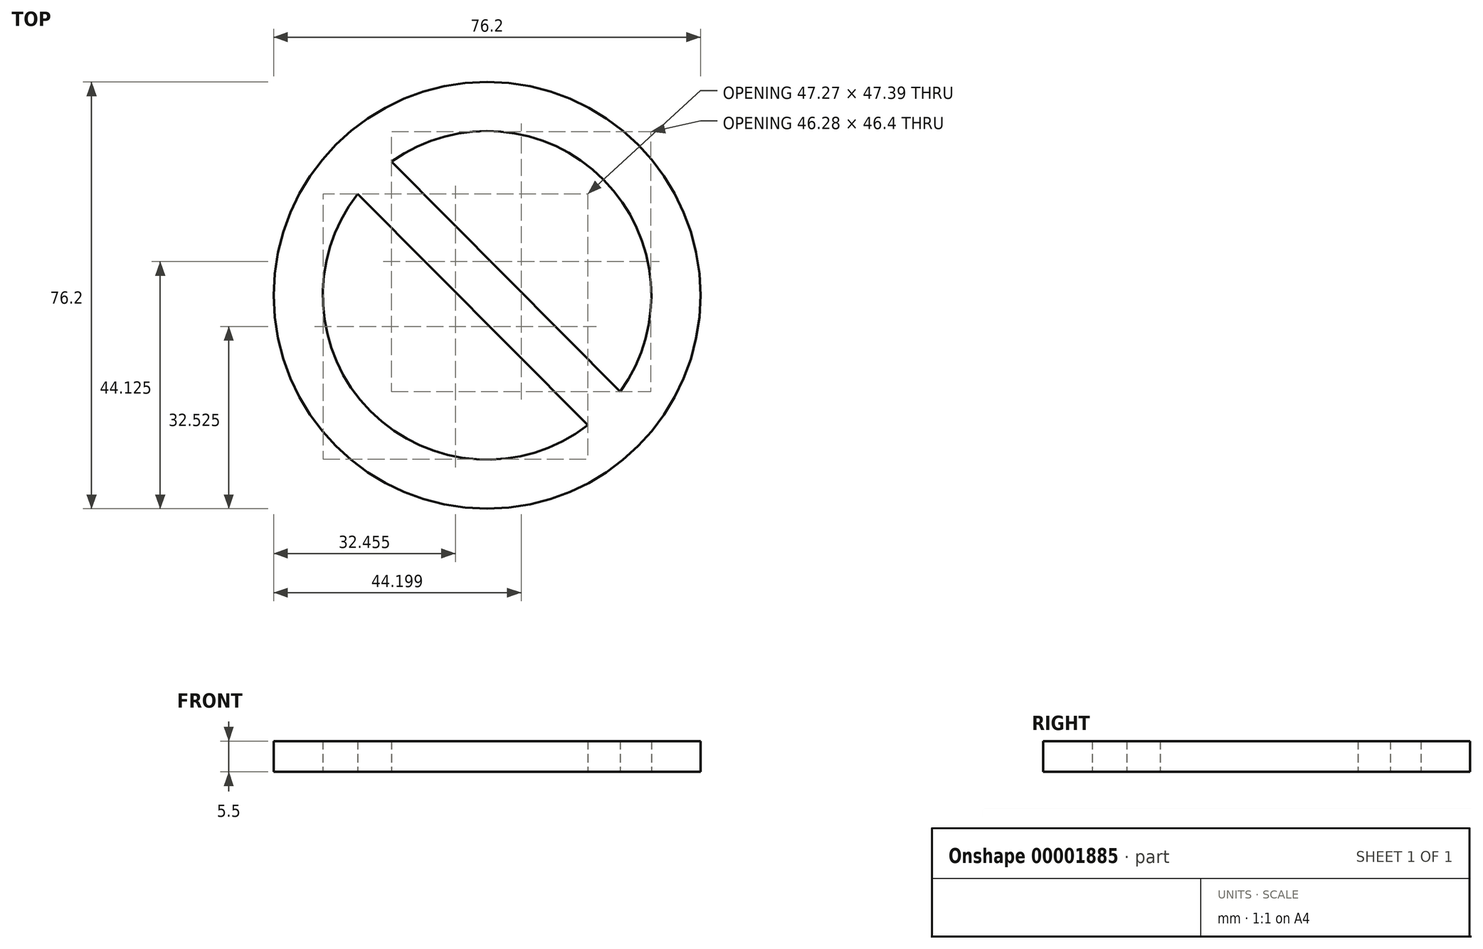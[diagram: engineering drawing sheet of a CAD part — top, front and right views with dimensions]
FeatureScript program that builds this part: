
annotation { "Feature Type Name" : "Feature", "Feature Type Description" : "" }
export const myFeature = defineFeature(function(context is Context, id is Id, definition is map)
    precondition{}
    {
        {
            var Q0;
            Q0=qCreatedBy(makeId("Top.planeOp"), FACE);
            var sketch = newSketch(context, id + "F0", { "sketchPlane" : qUnion([Q0])});
            skCircle(sketch, "E0", {"center": v(0, 0) * mm, "radius": 38.1 * mm});
            skArc(sketch, "E1", {"start": v(-23.06, 18.12) * mm, "mid": v(-20.8, -20.68) * mm, "end": v(18, -23.16) * mm});
            skLineSegment(sketch, "E2", {"start": v(-23.06, 18.12) * mm, "end": v(18, -23.16) * mm});
            skLineSegment(sketch, "E3", {"start": v(-17.04, 23.87) * mm, "end": v(23.77, -17.18) * mm});
            skArc(sketch, "E4.trimOffspring", {"start": v(23.77, -17.18) * mm, "mid": v(20.8, 20.68) * mm, "end": v(-17.04, 23.87) * mm});
            skSolve(sketch);
        }
        {
            var Q0;
            Q0 = qSketchRegion(id + "F0", true);
            extrude(context, id + "F1", {"entities" : qUnion([Q0]), "depth" : 5.5 * mm, "offsetDistance" : 25 * mm});
        }
    });
